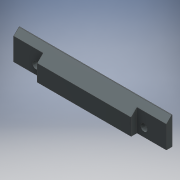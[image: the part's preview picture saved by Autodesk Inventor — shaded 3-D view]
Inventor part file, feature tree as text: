
AUTODESK INVENTOR PART (.ipt)
format: ipt  version: 2016 (Build 200138000, 138)  size: 177,664 bytes
history: native  units: mm
features: extrude x7, sketch x7, projected_geometry x4
ambient origin geometry x8: Origin, YZ Plane, XZ Plane, XY Plane, X Axis, Y Axis, Z Axis, Center Point
bodies: Solid1 (feature_tree)
feature tree (18):
  extrude  "Extrusion1"  TaperAngle=45.0deg  [1 undecoded]
  extrude  "Extrusion2"  Depth=130.0mm
  extrude  "Extrusion4"  Depth=25.0mm TaperAngle=0.0deg
  extrude  "Extrusion5"  Depth=6.0mm
  extrude  "Extrusion6"  Depth=13.0mm
  extrude  "Extrusion7"  Depth=6.0mm
  extrude  "Extrusion8"  Depth=5.0mm
  sketch  "Sketch1"  dims[d1=5.0mm d2=45.0deg]
  sketch  "Sketch2"  dims[d3=130.0mm d4=0.0mm d5=31.0mm]
  sketch  "Sketch3"  dims[d6=0.5mm d7=25.0mm d8=0.0mm]
  sketch  "Sketch4"  dims[d9=6.0mm d10=6.0mm]
  sketch  "Sketch5"  dims[d11=19.0mm d12=13.0mm]
  sketch  "Sketch6"  dims[d13=6.0mm d16=6.0mm]
  projected_geometry  "Projected Loop1"
  projected_geometry  "Projected Loop2"
  sketch  "Sketch7"  dims[d17=6.0mm d18=19.0mm d19=13.0mm d20=25.0mm d21=0.0mm d22=25.0mm d23=25.0mm d24=5.0mm d25=0.0mm d26=5.0mm d27=5.0mm d28=0.0mm d29=12.0mm d30=5.0mm d31=5.0mm d32=0.0mm d33=5.0mm d34=0.0mm]
  projected_geometry  "Projected Loop3"
  projected_geometry  "Projected Loop4"
note: 1 required parameter value undecoded (feature->parameter linkage not recoverable at this tier; creation-order binding heuristic only, values carry confidence <= 0.55)
